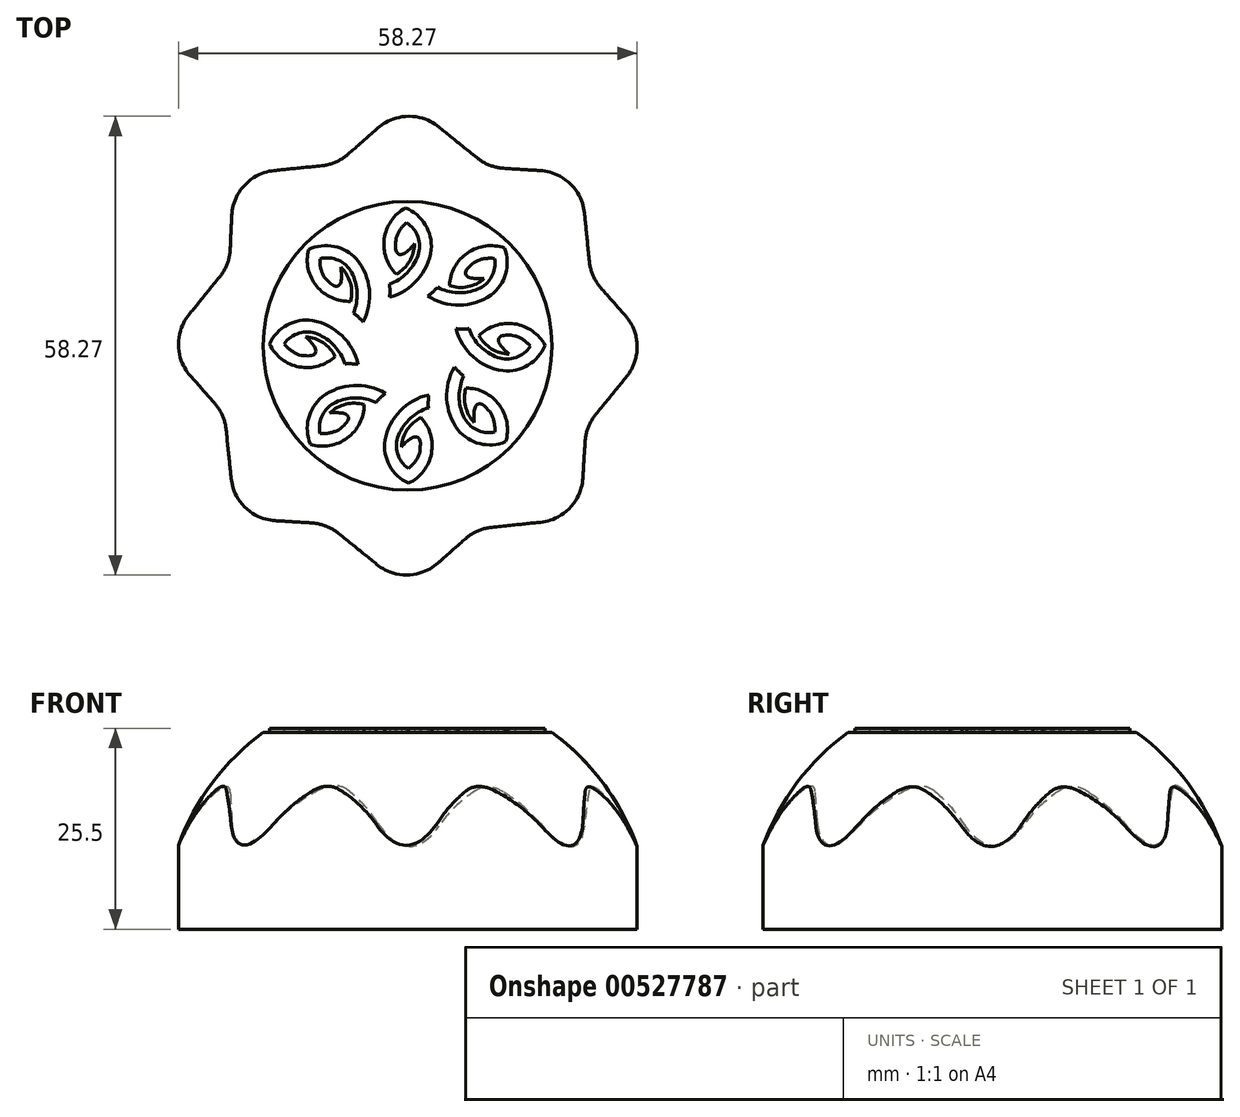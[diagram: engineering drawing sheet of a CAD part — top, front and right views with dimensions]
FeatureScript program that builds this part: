
annotation { "Feature Type Name" : "Feature", "Feature Type Description" : "" }
export const myFeature = defineFeature(function(context is Context, id is Id, definition is map)
    precondition{}
    {
        {
            var Q0;
            Q0=qCreatedBy(makeId("Top.planeOp"),FACE);
            var sketch = newSketch(context, id + "F0", { "sketchPlane" : qUnion([Q0])});
            skLineSegment(sketch, "E0", {"start": v(-3.79, 27.66) * mm, "end": v(-7.53, 24.36) * mm});
            skLineSegment(sketch, "E1", {"start": v(-10.89, 22.89) * mm, "end": v(-16.95, 22.27) * mm});
            skLineSegment(sketch, "E2", {"start": v(-22.53, 12.27) * mm, "end": v(-22.34, 16.57) * mm});
            skLineSegment(sketch, "E3", {"start": v(-23.87, 8.75) * mm, "end": v(-27.76, 3.97) * mm});
            skLineSegment(sketch, "E4", {"start": v(-24.52, -7.29) * mm, "end": v(-27.6, -3.79) * mm});
            skLineSegment(sketch, "E5", {"start": v(-23.05, -10.64) * mm, "end": v(-22.41, -16.83) * mm});
            skLineSegment(sketch, "E6", {"start": v(-16.82, -22.2) * mm, "end": v(-12.16, -22.5) * mm});
            skLineSegment(sketch, "E7", {"start": v(-8.74, -23.83) * mm, "end": v(-3.92, -27.76) * mm});
            skLineSegment(sketch, "E8", {"start": v(3.84, -27.6) * mm, "end": v(7.34, -24.52) * mm});
            skLineSegment(sketch, "E9", {"start": v(10.7, -23.05) * mm, "end": v(16.89, -22.41) * mm});
            skLineSegment(sketch, "E10", {"start": v(22.26, -16.82) * mm, "end": v(22.55, -12.16) * mm});
            skLineSegment(sketch, "E11", {"start": v(23.89, -8.74) * mm, "end": v(27.81, -3.92) * mm});
            skLineSegment(sketch, "E12", {"start": v(27.66, 3.84) * mm, "end": v(24.57, 7.34) * mm});
            skLineSegment(sketch, "E13", {"start": v(23.1, 10.7) * mm, "end": v(22.47, 16.89) * mm});
            skLineSegment(sketch, "E14", {"start": v(16.87, 22.26) * mm, "end": v(12.21, 22.55) * mm});
            skLineSegment(sketch, "E15", {"start": v(8.8, 23.89) * mm, "end": v(3.97, 27.82) * mm});
            skPoint(sketch, "E16.visualSharp", {"position": v(-8.97, 23.08) * mm});
            skArc(sketch, "E16.filletArc", {"start": v(-10.89, 22.89) * mm, "mid": v(-9.1, 23.36) * mm, "end": v(-7.53, 24.36) * mm});
            skPoint(sketch, "E17.visualSharp", {"position": v(0.03, 31.03) * mm});
            skArc(sketch, "E17.filletArc", {"start": v(3.97, 27.82) * mm, "mid": v(0.06, 29.16) * mm, "end": v(-3.79, 27.66) * mm});
            skPoint(sketch, "E18.visualSharp", {"position": v(10.29, 22.67) * mm});
            skArc(sketch, "E18.filletArc", {"start": v(8.8, 23.89) * mm, "mid": v(10.4, 22.95) * mm, "end": v(12.21, 22.55) * mm});
            skPoint(sketch, "E19.visualSharp", {"position": v(21.95, 21.95) * mm});
            skArc(sketch, "E19.filletArc", {"start": v(22.47, 16.89) * mm, "mid": v(20.65, 20.6) * mm, "end": v(16.87, 22.26) * mm});
            skPoint(sketch, "E20.visualSharp", {"position": v(23.3, 8.78) * mm});
            skArc(sketch, "E20.filletArc", {"start": v(23.1, 10.7) * mm, "mid": v(23.57, 8.9) * mm, "end": v(24.57, 7.34) * mm});
            skPoint(sketch, "E21.visualSharp", {"position": v(31.03, 0.03) * mm});
            skArc(sketch, "E21.filletArc", {"start": v(27.81, -3.92) * mm, "mid": v(29.16, 0) * mm, "end": v(27.66, 3.84) * mm});
            skPoint(sketch, "E22.visualSharp", {"position": v(21.95, -21.9) * mm});
            skArc(sketch, "E22.filletArc", {"start": v(16.89, -22.41) * mm, "mid": v(20.6, -20.6) * mm, "end": v(22.26, -16.82) * mm});
            skPoint(sketch, "E23.visualSharp", {"position": v(0.03, -30.97) * mm});
            skArc(sketch, "E23.filletArc", {"start": v(-3.92, -27.76) * mm, "mid": v(-0.01, -29.1) * mm, "end": v(3.84, -27.6) * mm});
            skPoint(sketch, "E24.visualSharp", {"position": v(-21.9, -21.9) * mm});
            skArc(sketch, "E24.filletArc", {"start": v(-22.41, -16.83) * mm, "mid": v(-20.6, -20.55) * mm, "end": v(-16.82, -22.2) * mm});
            skPoint(sketch, "E25.visualSharp", {"position": v(-30.97, 0.03) * mm});
            skArc(sketch, "E25.filletArc", {"start": v(-27.76, 3.97) * mm, "mid": v(-29.1, 0.06) * mm, "end": v(-27.6, -3.79) * mm});
            skPoint(sketch, "E26.visualSharp", {"position": v(-22.1, 21.74) * mm});
            skArc(sketch, "E26.filletArc", {"start": v(-16.95, 22.27) * mm, "mid": v(-20.7, 20.42) * mm, "end": v(-22.34, 16.57) * mm});
            skPoint(sketch, "E27.visualSharp", {"position": v(-23.24, -8.73) * mm});
            skArc(sketch, "E27.filletArc", {"start": v(-23.05, -10.64) * mm, "mid": v(-23.52, -8.85) * mm, "end": v(-24.52, -7.29) * mm});
            skPoint(sketch, "E28.visualSharp", {"position": v(-10.24, -22.62) * mm});
            skArc(sketch, "E28.filletArc", {"start": v(-8.74, -23.83) * mm, "mid": v(-10.35, -22.9) * mm, "end": v(-12.16, -22.5) * mm});
            skPoint(sketch, "E29.visualSharp", {"position": v(8.78, -23.24) * mm});
            skArc(sketch, "E29.filletArc", {"start": v(10.7, -23.05) * mm, "mid": v(8.9, -23.52) * mm, "end": v(7.34, -24.52) * mm});
            skPoint(sketch, "E30.visualSharp", {"position": v(22.67, -10.23) * mm});
            skArc(sketch, "E30.filletArc", {"start": v(23.89, -8.74) * mm, "mid": v(22.95, -10.34) * mm, "end": v(22.55, -12.16) * mm});
            skPoint(sketch, "E31.visualSharp", {"position": v(-22.62, 10.29) * mm});
            skArc(sketch, "E31.filletArc", {"start": v(-23.87, 8.75) * mm, "mid": v(-22.92, 10.4) * mm, "end": v(-22.53, 12.27) * mm});
            skSolve(sketch);
        }
        {
            var Q0;
            Q0=qCreatedBy(makeId("Front.planeOp"),FACE);
            var sketch = newSketch(context, id + "F1", { "sketchPlane" : qUnion([Q0])});
            skArc(sketch, "E32", {"start": v(31, 0) * mm, "mid": v(21.92, 21.92) * mm, "end": v(0, 31) * mm});
            skLineSegment(sketch, "E33", {"start": v(0, 0) * mm, "end": v(31, 0) * mm});
            skLineSegment(sketch, "E34", {"start": v(0, 0) * mm, "end": v(0, 31) * mm});
            skSolve(sketch);
        }
        {
            var Q0;
            Q0=makeQuery(id+"F1.imprint","IMPRINT",FACE,{"disambiguationData":[TD([[makeQuery(id+"F1.imprint","IMPRINT",EDGE,{"derivedFrom":sQuery(id+"F1.wireOp",EDGE,"E32")}),1.0]])]});
            var Q1;
            Q1=sQuery(id+"F1.wireOp",EDGE,"E34");
            revolve(context, id + "F2", {"entities" : qUnion([Q0]), "axis" : qUnion([Q1]), "revolveType" : RevolveType.FULL});
        }
        {
            var Q0;
            Q0 = qSketchRegion(id + "F0", true);
            extrude(context, id + "F3", {"entities" : qUnion([Q0]), "operationType" : NewBodyOperationType.INTERSECT, "depth" : 25 * mm, "offsetDistance" : 25 * mm});
        }
        {
            var Q0;
            Q0=qCreatedBy(makeId("Top.planeOp"),FACE);
            var sketch = newSketch(context, id + "F4", { "sketchPlane" : qUnion([Q0])});
            skArc(sketch, "E35", {"start": v(-17.53, 0.22) * mm, "mid": v(-13.76, -2.67) * mm, "end": v(-9.2, -1.36) * mm});
            skArc(sketch, "E36", {"start": v(-12.06, 3.22) * mm, "mid": v(-15.3, 2.63) * mm, "end": v(-17.53, 0.22) * mm});
            skArc(sketch, "E37", {"start": v(-6.3, -2.36) * mm, "mid": v(-8.34, 1.3) * mm, "end": v(-12.06, 3.22) * mm});
            skArc(sketch, "E38", {"start": v(-6.3, -2.36) * mm, "mid": v(-7.13, -2.28) * mm, "end": v(-7.97, -2.29) * mm});
            skArc(sketch, "E39", {"start": v(-7.97, -2.29) * mm, "mid": v(-9.28, -0.01) * mm, "end": v(-11.43, 1.5) * mm});
            skArc(sketch, "E40", {"start": v(-11.43, 1.5) * mm, "mid": v(-13.77, 1.62) * mm, "end": v(-15.68, 0.25) * mm});
            skArc(sketch, "E41", {"start": v(-15.68, 0.25) * mm, "mid": v(-14.82, -0.58) * mm, "end": v(-13.76, -1.15) * mm});
            skArc(sketch, "E42", {"start": v(-9.2, -1.36) * mm, "mid": v(-10.73, 0.39) * mm, "end": v(-12.94, 1.15) * mm});
            skFitSpline(sketch, "E43", {"points": [v(-13.76, -1.15) * mm, v(-12.94, -1.26) * mm, v(-12.08, -1.22) * mm, v(-11.72, -0.95) * mm, v(-11.67, -0.46) * mm, v(-11.96, 0.08) * mm, v(-12.35, 0.57) * mm, v(-12.94, 1.15) * mm], "startDerivative": vector(7.77, -1.7) * mm, "endDerivative": vector(-3.9, 3.72) * mm});
            skArc(sketch, "E44", {"start": v(-12.34, -12.51) * mm, "mid": v(-7.66, -11.71) * mm, "end": v(-5.51, -7.47) * mm});
            skArc(sketch, "E45", {"start": v(-10.82, -6.46) * mm, "mid": v(-12.59, -9.23) * mm, "end": v(-12.34, -12.51) * mm});
            skArc(sketch, "E46", {"start": v(-2.81, -6.03) * mm, "mid": v(-6.88, -5.04) * mm, "end": v(-10.82, -6.46) * mm});
            skArc(sketch, "E47", {"start": v(-2.81, -6.03) * mm, "mid": v(-3.44, -6.58) * mm, "end": v(-4, -7.2) * mm});
            skArc(sketch, "E48", {"start": v(-4, -7.2) * mm, "mid": v(-6.56, -6.62) * mm, "end": v(-9.13, -7.17) * mm});
            skArc(sketch, "E49", {"start": v(-9.13, -7.17) * mm, "mid": v(-10.81, -8.8) * mm, "end": v(-11.1, -11.13) * mm});
            skArc(sketch, "E50", {"start": v(-11.1, -11.13) * mm, "mid": v(-9.9, -11.07) * mm, "end": v(-8.77, -10.68) * mm});
            skArc(sketch, "E51", {"start": v(-5.51, -7.47) * mm, "mid": v(-7.84, -7.41) * mm, "end": v(-9.9, -8.51) * mm});
            skFitSpline(sketch, "E52", {"points": [v(-8.77, -10.68) * mm, v(-8.14, -10.15) * mm, v(-7.58, -9.5) * mm, v(-7.53, -9.04) * mm, v(-7.86, -8.68) * mm, v(-8.45, -8.52) * mm, v(-9.07, -8.48) * mm, v(-9.9, -8.51) * mm], "startDerivative": vector(6.53, 4.54) * mm, "endDerivative": vector(-5.38, -0.34) * mm});
            skArc(sketch, "E53", {"start": v(-12.58, 12.23) * mm, "mid": v(-11.55, 7.59) * mm, "end": v(-7.21, 5.65) * mm});
            skArc(sketch, "E54", {"start": v(-6.47, 11) * mm, "mid": v(-9.32, 12.63) * mm, "end": v(-12.58, 12.23) * mm});
            skArc(sketch, "E55", {"start": v(-5.64, 3.03) * mm, "mid": v(-4.85, 7.14) * mm, "end": v(-6.47, 11) * mm});
            skArc(sketch, "E56", {"start": v(-5.64, 3.03) * mm, "mid": v(-6.22, 3.62) * mm, "end": v(-6.87, 4.15) * mm});
            skArc(sketch, "E57", {"start": v(-6.87, 4.15) * mm, "mid": v(-6.41, 6.74) * mm, "end": v(-7.1, 9.28) * mm});
            skArc(sketch, "E58", {"start": v(-7.1, 9.28) * mm, "mid": v(-8.8, 10.88) * mm, "end": v(-11.14, 11.06) * mm});
            skArc(sketch, "E59", {"start": v(-11.14, 11.06) * mm, "mid": v(-11.02, 9.86) * mm, "end": v(-10.58, 8.75) * mm});
            skArc(sketch, "E60", {"start": v(-7.21, 5.65) * mm, "mid": v(-7.27, 7.98) * mm, "end": v(-8.47, 9.98) * mm});
            skFitSpline(sketch, "E61", {"points": [v(-10.58, 8.75) * mm, v(-10.02, 8.14) * mm, v(-9.34, 7.62) * mm, v(-8.88, 7.6) * mm, v(-8.53, 7.93) * mm, v(-8.4, 8.54) * mm, v(-8.4, 9.16) * mm, v(-8.47, 9.98) * mm], "startDerivative": vector(4.85, -6.3) * mm, "endDerivative": vector(-0.6, 5.36) * mm});
            skArc(sketch, "E62", {"start": v(17.47, 0.05) * mm, "mid": v(13.58, 2.8) * mm, "end": v(9.07, 1.3) * mm});
            skArc(sketch, "E63", {"start": v(12.12, -3.16) * mm, "mid": v(15.33, -2.44) * mm, "end": v(17.47, 0.05) * mm});
            skArc(sketch, "E64", {"start": v(6.14, 2.18) * mm, "mid": v(8.33, -1.4) * mm, "end": v(12.12, -3.16) * mm});
            skArc(sketch, "E65", {"start": v(6.14, 2.18) * mm, "mid": v(6.97, 2.14) * mm, "end": v(7.8, 2.18) * mm});
            skArc(sketch, "E66", {"start": v(7.8, 2.18) * mm, "mid": v(9.2, -0.04) * mm, "end": v(11.42, -1.46) * mm});
            skArc(sketch, "E67", {"start": v(11.42, -1.46) * mm, "mid": v(13.76, -1.5) * mm, "end": v(15.61, -0.05) * mm});
            skArc(sketch, "E68", {"start": v(15.61, -0.05) * mm, "mid": v(14.72, 0.75) * mm, "end": v(13.64, 1.27) * mm});
            skArc(sketch, "E69", {"start": v(9.07, 1.3) * mm, "mid": v(10.68, -0.39) * mm, "end": v(12.91, -1.05) * mm});
            skFitSpline(sketch, "E70", {"points": [v(13.64, 1.27) * mm, v(12.82, 1.35) * mm, v(11.96, 1.28) * mm, v(11.6, 0.99) * mm, v(11.58, 0.5) * mm, v(11.9, -0.03) * mm, v(12.3, -0.5) * mm, v(12.91, -1.05) * mm], "startDerivative": vector(-7.83, 1.4) * mm, "endDerivative": vector(4.05, -3.56) * mm});
            skArc(sketch, "E71", {"start": v(12.33, 12.43) * mm, "mid": v(7.62, 11.8) * mm, "end": v(5.32, 7.65) * mm});
            skArc(sketch, "E72", {"start": v(10.59, 6.44) * mm, "mid": v(12.46, 9.15) * mm, "end": v(12.33, 12.43) * mm});
            skArc(sketch, "E73", {"start": v(2.57, 6.31) * mm, "mid": v(6.6, 5.17) * mm, "end": v(10.59, 6.44) * mm});
            skArc(sketch, "E74", {"start": v(2.57, 6.31) * mm, "mid": v(3.2, 6.85) * mm, "end": v(3.8, 7.44) * mm});
            skArc(sketch, "E75", {"start": v(3.8, 7.44) * mm, "mid": v(6.33, 6.76) * mm, "end": v(8.92, 7.22) * mm});
            skArc(sketch, "E76", {"start": v(8.92, 7.22) * mm, "mid": v(10.66, 8.78) * mm, "end": v(11.04, 11.1) * mm});
            skArc(sketch, "E77", {"start": v(11.04, 11.1) * mm, "mid": v(9.84, 11.08) * mm, "end": v(8.7, 10.74) * mm});
            skArc(sketch, "E78", {"start": v(5.32, 7.65) * mm, "mid": v(7.64, 7.5) * mm, "end": v(9.74, 8.53) * mm});
            skFitSpline(sketch, "E79", {"points": [v(8.7, 10.74) * mm, v(8.04, 10.23) * mm, v(7.46, 9.6) * mm, v(7.4, 9.15) * mm, v(7.7, 8.77) * mm, v(8.3, 8.6) * mm, v(8.91, 8.53) * mm, v(9.74, 8.53) * mm], "startDerivative": vector(-6.7, -4.28) * mm, "endDerivative": vector(5.39, 0.13) * mm});
            skArc(sketch, "E80", {"start": v(-0.27, 17.51) * mm, "mid": v(-2.97, 13.6) * mm, "end": v(-1.43, 9.1) * mm});
            skArc(sketch, "E81", {"start": v(3, 12.2) * mm, "mid": v(2.25, 15.4) * mm, "end": v(-0.27, 17.51) * mm});
            skArc(sketch, "E82", {"start": v(-2.28, 6.17) * mm, "mid": v(1.27, 8.4) * mm, "end": v(3, 12.2) * mm});
            skArc(sketch, "E83", {"start": v(-2.28, 6.17) * mm, "mid": v(-2.25, 7) * mm, "end": v(-2.3, 7.83) * mm});
            skArc(sketch, "E84", {"start": v(-2.3, 7.83) * mm, "mid": v(-0.09, 9.26) * mm, "end": v(1.3, 11.48) * mm});
            skArc(sketch, "E85", {"start": v(1.3, 11.48) * mm, "mid": v(1.32, 13.83) * mm, "end": v(-0.15, 15.66) * mm});
            skArc(sketch, "E86", {"start": v(-0.15, 15.66) * mm, "mid": v(-0.94, 14.76) * mm, "end": v(-1.45, 13.68) * mm});
            skArc(sketch, "E87", {"start": v(-1.43, 9.1) * mm, "mid": v(0.24, 10.73) * mm, "end": v(0.88, 12.97) * mm});
            skFitSpline(sketch, "E88", {"points": [v(-1.45, 13.68) * mm, v(-1.52, 12.86) * mm, v(-1.44, 12) * mm, v(-1.15, 11.65) * mm, v(-0.66, 11.63) * mm, v(-0.13, 11.94) * mm, v(0.33, 12.36) * mm, v(0.88, 12.97) * mm], "startDerivative": vector(-1.31, -7.84) * mm, "endDerivative": vector(3.52, 4.09) * mm});
            skArc(sketch, "E89", {"start": v(0.13, -17.45) * mm, "mid": v(3.02, -13.68) * mm, "end": v(1.71, -9.11) * mm});
            skArc(sketch, "E90", {"start": v(-2.87, -11.98) * mm, "mid": v(-2.28, -15.21) * mm, "end": v(0.13, -17.45) * mm});
            skArc(sketch, "E91", {"start": v(2.71, -6.22) * mm, "mid": v(-0.95, -8.26) * mm, "end": v(-2.87, -11.98) * mm});
            skArc(sketch, "E92", {"start": v(2.71, -6.22) * mm, "mid": v(2.63, -7.05) * mm, "end": v(2.64, -7.88) * mm});
            skArc(sketch, "E93", {"start": v(2.64, -7.88) * mm, "mid": v(0.36, -9.2) * mm, "end": v(-1.14, -11.35) * mm});
            skArc(sketch, "E94", {"start": v(-1.14, -11.35) * mm, "mid": v(-1.27, -13.69) * mm, "end": v(0.1, -15.6) * mm});
            skArc(sketch, "E95", {"start": v(0.1, -15.6) * mm, "mid": v(0.94, -14.74) * mm, "end": v(1.5, -13.68) * mm});
            skArc(sketch, "E96", {"start": v(1.71, -9.11) * mm, "mid": v(-0.04, -10.65) * mm, "end": v(-0.8, -12.86) * mm});
            skFitSpline(sketch, "E97", {"points": [v(1.5, -13.68) * mm, v(1.6, -12.86) * mm, v(1.57, -12) * mm, v(1.3, -11.64) * mm, v(0.81, -11.59) * mm, v(0.27, -11.88) * mm, v(-0.21, -12.27) * mm, v(-0.8, -12.86) * mm], "startDerivative": vector(1.7, 7.77) * mm, "endDerivative": vector(-3.72, -3.9) * mm});
            skArc(sketch, "E98", {"start": v(12.46, -12.18) * mm, "mid": v(11.65, -7.5) * mm, "end": v(7.4, -5.36) * mm});
            skArc(sketch, "E99", {"start": v(6.4, -10.67) * mm, "mid": v(9.18, -12.43) * mm, "end": v(12.46, -12.18) * mm});
            skArc(sketch, "E100", {"start": v(5.96, -2.66) * mm, "mid": v(4.98, -6.74) * mm, "end": v(6.4, -10.67) * mm});
            skArc(sketch, "E101", {"start": v(5.96, -2.66) * mm, "mid": v(6.51, -3.29) * mm, "end": v(7.13, -3.84) * mm});
            skArc(sketch, "E102", {"start": v(7.13, -3.84) * mm, "mid": v(6.55, -6.4) * mm, "end": v(7.11, -8.97) * mm});
            skArc(sketch, "E103", {"start": v(7.11, -8.97) * mm, "mid": v(8.75, -10.65) * mm, "end": v(11.07, -10.94) * mm});
            skArc(sketch, "E104", {"start": v(11.07, -10.94) * mm, "mid": v(11.01, -9.74) * mm, "end": v(10.62, -8.61) * mm});
            skArc(sketch, "E105", {"start": v(7.4, -5.36) * mm, "mid": v(7.35, -7.69) * mm, "end": v(8.46, -9.74) * mm});
            skFitSpline(sketch, "E106", {"points": [v(10.62, -8.61) * mm, v(10.09, -7.98) * mm, v(9.43, -7.42) * mm, v(8.98, -7.37) * mm, v(8.62, -7.7) * mm, v(8.46, -8.3) * mm, v(8.42, -8.92) * mm, v(8.46, -9.74) * mm], "startDerivative": vector(-4.55, 6.52) * mm, "endDerivative": vector(0.35, -5.38) * mm});
            skSolve(sketch);
        }
        {
            var Q0;
            Q0 = qSketchRegion(id + "F4", true);
            extrude(context, id + "F5", {"entities" : qUnion([Q0]), "operationType" : NewBodyOperationType.ADD, "depth" : 25.5 * mm, "offsetDistance" : 25 * mm});
        }
    });
